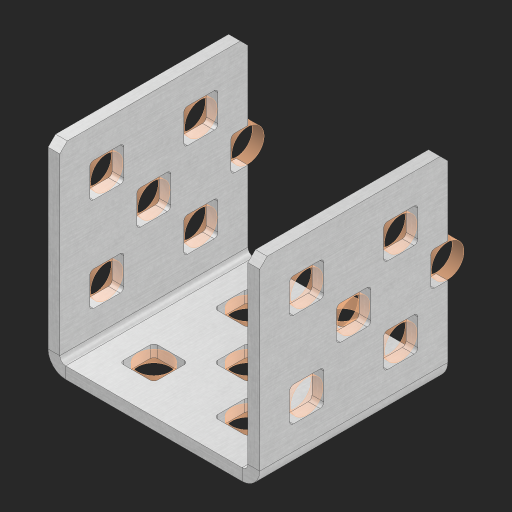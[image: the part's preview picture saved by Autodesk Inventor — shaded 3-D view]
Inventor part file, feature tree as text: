
AUTODESK INVENTOR PART (.ipt)
format: ipt  version: 2023 (Build 270158000, 158)  size: 665,088 bytes
history: native  units: in
note: dims shown in document units (in); Inventor stores cm internally (conversion verified against a paired STEP export)
features: other x30, extrude x22, sheet_metal_op x8, sketch x7, mirror x3, pattern_linear x2, chamfer x1
ambient origin geometry x8: Origin, YZ Plane, XZ Plane, XY Plane, X Axis, Y Axis, Z Axis, Center Point
bodies: Solid1 (feature_tree), Body (feature_tree)
feature tree (73):
  sheet_metal_op  "Flanges"
  sheet_metal_op  "Body Pattern"
  pattern_linear  "Center Pattern"  Spacing1=1.0in  [1 undecoded]
  other  "Arc Length"
  mirror  "Notch Mirror"
  pattern_linear  "Notch Pattern"  Spacing1=0.25in  [1 undecoded]
  other  "Diagonal Plane"
  mirror  "Flange 1"
  mirror  "Flange 2"
  chamfer  "End Chamfer"
  sketch  "Sketch1"  dims[d0=1.0in]
  other  "Plate1"
  sketch  "Sketch2"  dims[d1=1.0in]
  other  "Plate2"
  sheet_metal_op  "Bend1"
  sheet_metal_op  "Corner1"
  sketch  "Sketch8"  dims[d2=0.0625in]
  sketch  "Sketch9"  dims[d3=0.0625in]
  other  "Srf91"
  sheet_metal_op  "Body Pattern Sketch"
  other  "Srf92"
  sketch  "Sketch13"  dims[d4=0.0312in]
  sketch  "Sketch15"  dims[d5=0.125in]
  sketch  "Sketch16"  dims[d6=0.0625in d7=1.0in d8=90.0deg d9=0.0312in d10=0.25in d11=0.0625in d12=0.0625in d49=0.182in d50=0.02in d52=0.25in d53=0.0625in d54=0.0in d55=0.172in d56=1.0in d57=0.0in d60=0.7874in d62=0.5in d63=0.7874in d65=0.5in d85=0.1473in d86=0.1782in d88=0.04in d89=0.0625in d90=0.0in d91=0.04in d92=0.0491in d95=2.5in d96=0.04in d97=0.25in d98=45.0deg d99=0.25in d102=2.497in d106=0.182in d107=0.02in d108=0.5in d110=0.0625in d111=0.0in d112=0.172in d113=0.5in d114=0.0in d117=0.5in d118=0.5in d131=0.25in d132=0.25in]
  other  "Srf786"
  other  "Srf889"
  other  "Srf1315"
  other  "Srf1316"
  other  "Srf1317"
  other  "Srf1325"
  other  "Srf1374"
  other  "Srf1375"
  other  "Srf1376"
  other  "Srf1384"
  other  "Srf1433"
  other  "Srf1434"
  other  "Srf1473"
  other  "Srf1474"
  other  "Srf1500"
  other  "Srf1501"
  other  "Srf1538"
  other  "Srf1539"
  other  "Srf1576"
  other  "Srf1577"
  other  "Srf1614"
  other  "Srf1615"
  sheet_metal_op  "Body Stamp"
  sheet_metal_op  "Body Circle"
  other  "Center Stamp"
  other  "Center Circle"
  sheet_metal_op  "Notch"
  extrude  "ExtrusionSrf92"  Depth=0.0625in
  extrude  "ExtrusionSrf889"  Depth=0.0625in
  extrude  "ExtrusionSrf1315"  Depth=0.182in
  extrude  "ExtrusionSrf1316"  Depth=0.02in
  extrude  "ExtrusionSrf1355"  Depth=0.25in
  extrude  "ExtrusionSrf1356"  Depth=0.0625in
  extrude  "ExtrusionSrf1374"  TaperAngle=0.0deg  [1 undecoded]
  extrude  "ExtrusionSrf1375"  Depth=0.25in
  extrude  "ExtrusionSrf1414"  Depth=1.0in TaperAngle=0.0deg
  extrude  "ExtrusionSrf1415"  Depth=0.25in
  extrude  "ExtrusionSrf1433"  Depth=0.5in
  extrude  "ExtrusionSrf1434"  Depth=0.25in
  extrude  "ExtrusionSrf1473"  Depth=0.25in
  extrude  "ExtrusionSrf1474"  Depth=0.25in
  extrude  "ExtrusionSrf1500"  Depth=0.0625in
  extrude  "ExtrusionSrf1501"  TaperAngle=0.0deg  [1 undecoded]
  extrude  "ExtrusionSrf1538"  Depth=0.25in
  extrude  "ExtrusionSrf1539"  Depth=0.25in
  extrude  "ExtrusionSrf1576"  Depth=0.25in
  extrude  "ExtrusionSrf1577"  Depth=0.25in TaperAngle=45.0deg
  extrude  "ExtrusionSrf1614"  Depth=0.25in
  extrude  "ExtrusionSrf1615"  Depth=0.25in
note: 4 required parameter values undecoded (feature->parameter linkage not recoverable at this tier; creation-order binding heuristic only, values carry confidence <= 0.55)
